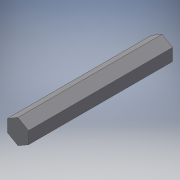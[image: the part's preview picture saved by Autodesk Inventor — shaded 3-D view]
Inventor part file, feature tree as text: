
AUTODESK INVENTOR PART (.ipt)
format: ipt  version: 2018 (Build 220112000, 112)  size: 94,208 bytes
history: native  units: in
note: dims shown in document units (in); Inventor stores cm internally (conversion verified against a paired STEP export)
features: extrude x1, sketch x1
ambient origin geometry x8: Origin, YZ Plane, XZ Plane, XY Plane, X Axis, Y Axis, Z Axis, Center Point
bodies: Solid1 (feature_tree)
feature tree (2):
  extrude  "Extrusion1"  Depth=3.4in TaperAngle=0.0deg
  sketch  "Sketch1"  dims[d0=0.25in d1=3.4in d2=0.0in]
